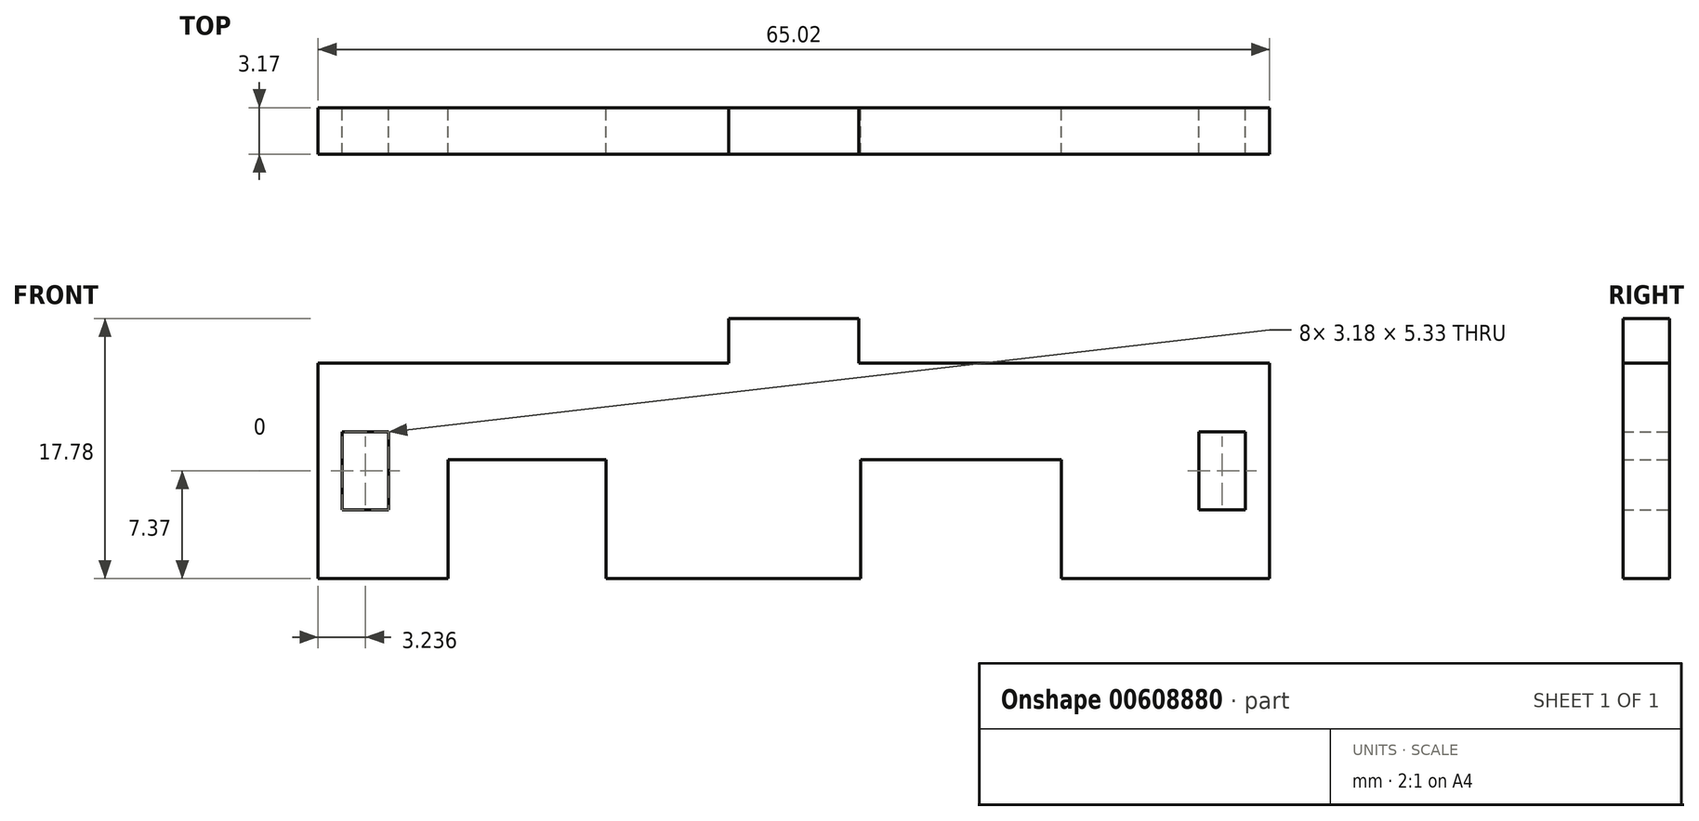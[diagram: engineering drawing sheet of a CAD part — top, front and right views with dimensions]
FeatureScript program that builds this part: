
annotation { "Feature Type Name" : "Feature", "Feature Type Description" : "" }
export const myFeature = defineFeature(function(context is Context, id is Id, definition is map)
    precondition{}
    {
        {
            var Q0;
            Q0=qCreatedBy(makeId("Front.planeOp"),FACE);
            var sketch = newSketch(context, id + "F0", { "sketchPlane" : qUnion([Q0])});
            skLineSegment(sketch, "E0.bottom", {"start": v(-32.51, -7.37) * mm, "end": v(-23.62, -7.37) * mm});
            skLineSegment(sketch, "E0.top", {"start": v(-32.51, 7.37) * mm, "end": v(-4.45, 7.37) * mm});
            skLineSegment(sketch, "E0.left", {"start": v(-32.51, -7.37) * mm, "end": v(-32.51, 7.37) * mm});
            skLineSegment(sketch, "E0.right", {"start": v(32.51, -7.37) * mm, "end": v(32.51, 7.37) * mm});
            skPoint(sketch, "E0.middle", {"position": v(0, 0) * mm});
            skLineSegment(sketch, "E1.0", {"start": v(-4.45, 10.41) * mm, "end": v(4.45, 10.41) * mm});
            skLineSegment(sketch, "E2.0", {"start": v(-4.45, 7.37) * mm, "end": v(-4.45, 10.41) * mm});
            skLineSegment(sketch, "E3.0", {"start": v(4.45, 7.37) * mm, "end": v(4.45, 10.41) * mm});
            skLineSegment(sketch, "E4.trimOffspring", {"start": v(4.45, 7.37) * mm, "end": v(32.51, 7.37) * mm});
            skLineSegment(sketch, "E5.0", {"start": v(-23.62, -7.37) * mm, "end": v(-23.62, 0.76) * mm});
            skLineSegment(sketch, "E6.0", {"start": v(-23.62, 0.76) * mm, "end": v(-12.83, 0.76) * mm});
            skLineSegment(sketch, "E7.0", {"start": v(-12.83, -7.37) * mm, "end": v(-12.83, 0.76) * mm});
            skLineSegment(sketch, "E8.trimOffspring", {"start": v(-12.83, -7.37) * mm, "end": v(4.57, -7.37) * mm});
            skLineSegment(sketch, "E9.0", {"start": v(4.57, -7.37) * mm, "end": v(4.57, 0.76) * mm});
            skLineSegment(sketch, "E10.0", {"start": v(18.29, -7.37) * mm, "end": v(18.29, 0.76) * mm});
            skLineSegment(sketch, "E11.trimOffspring", {"start": v(4.57, 0.76) * mm, "end": v(18.29, 0.76) * mm});
            skLineSegment(sketch, "E12.trimOffspring", {"start": v(18.29, -7.37) * mm, "end": v(32.51, -7.37) * mm});
            skLineSegment(sketch, "E13.0", {"start": v(-30.86, -2.67) * mm, "end": v(-30.86, 2.67) * mm});
            skLineSegment(sketch, "E14.0", {"start": v(30.86, -2.67) * mm, "end": v(30.86, 2.67) * mm});
            skLineSegment(sketch, "E15.0", {"start": v(27.69, -2.67) * mm, "end": v(27.69, 2.67) * mm});
            skLineSegment(sketch, "E16.0", {"start": v(-27.69, -2.67) * mm, "end": v(-27.69, 2.67) * mm});
            skLineSegment(sketch, "E17.0", {"start": v(-30.86, -2.67) * mm, "end": v(-27.69, -2.67) * mm});
            skLineSegment(sketch, "E18.0", {"start": v(27.69, -2.67) * mm, "end": v(30.86, -2.67) * mm});
            skLineSegment(sketch, "E19.0", {"start": v(27.69, 2.67) * mm, "end": v(30.86, 2.67) * mm});
            skLineSegment(sketch, "E20.0", {"start": v(-30.86, 2.67) * mm, "end": v(-27.69, 2.67) * mm});
            skSolve(sketch);
        }
        {
            var Q0;
            Q0=makeQuery(id+"F0.imprint","IMPRINT",FACE,{"disambiguationData":[TD([[makeQuery(id+"F0.imprint","IMPRINT",EDGE,{"derivedFrom":sQuery(id+"F0.wireOp",EDGE,"E0.bottom")}),1.0]])]});
            extrude(context, id + "F1", {"entities" : qUnion([Q0]), "depth" : 3.17 * mm, "offsetDistance" : 25.4 * mm});
        }
    });
